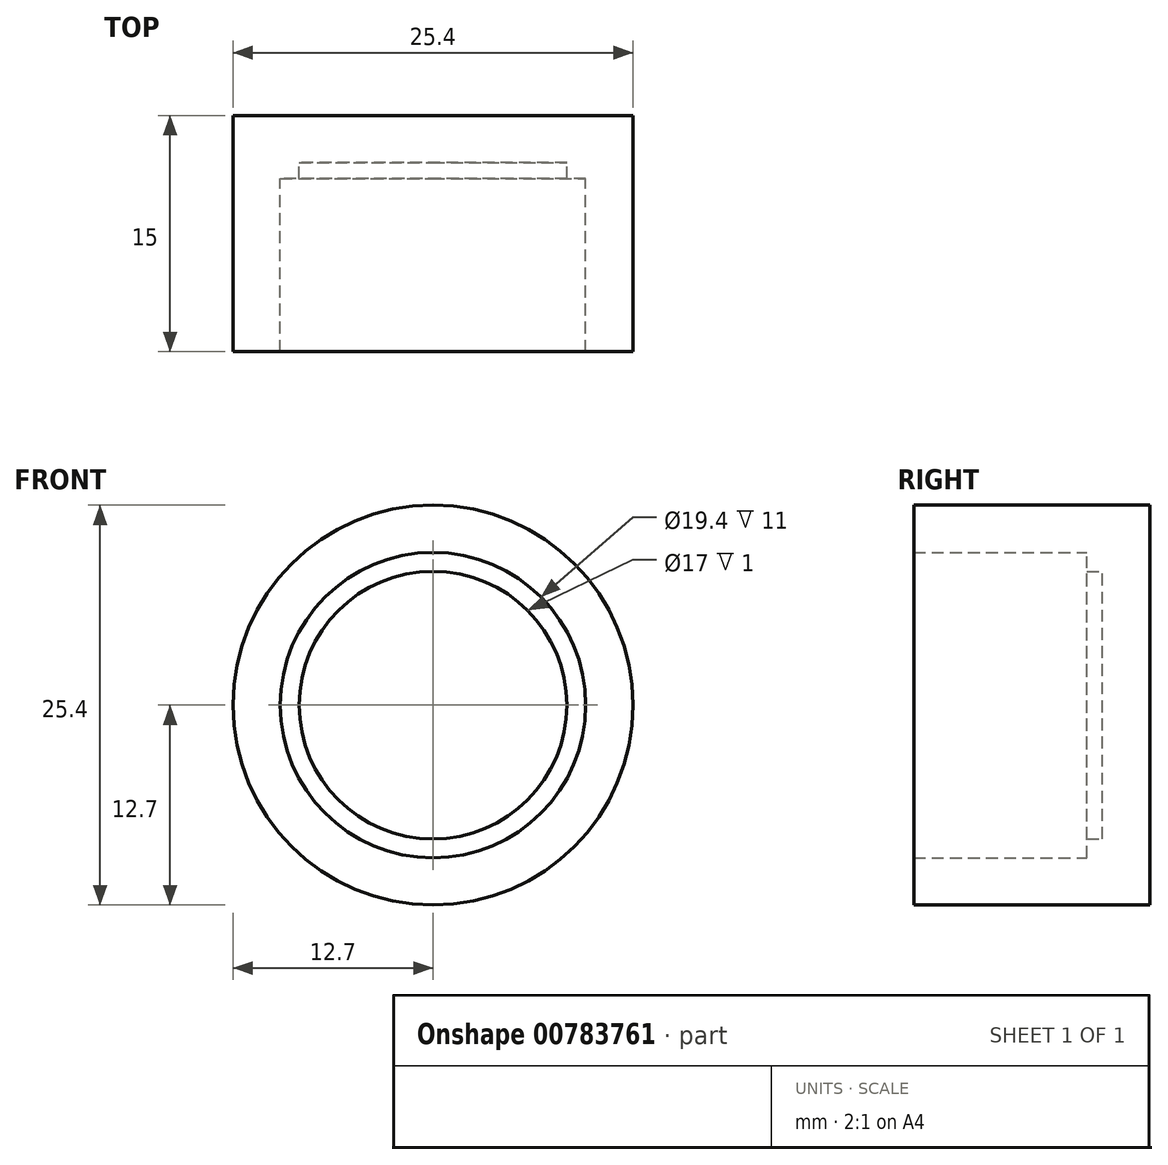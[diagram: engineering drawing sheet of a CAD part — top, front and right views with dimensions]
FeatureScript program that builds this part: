
annotation { "Feature Type Name" : "Feature", "Feature Type Description" : "" }
export const myFeature = defineFeature(function(context is Context, id is Id, definition is map)
    precondition{}
    {
        {
            var Q0;
            Q0=qCreatedBy(makeId("Front.planeOp"),FACE);
            var sketch = newSketch(context, id + "F0", { "sketchPlane" : qUnion([Q0])});
            skCircle(sketch, "E0", {"center": v(0, 0) * mm, "radius": 12.7 * mm});
            skCircle(sketch, "E1", {"center": v(0, 0) * mm, "radius": 9.7 * mm});
            skCircle(sketch, "E2", {"center": v(0, 0) * mm, "radius": 8.5 * mm});
            skSolve(sketch);
        }
        {
            var Q0;
            Q0=makeQuery(id+"F0.imprint","IMPRINT",FACE,{"disambiguationData":[TD([[makeQuery(id+"F0.imprint","IMPRINT",EDGE,{"derivedFrom":sQuery(id+"F0.wireOp",EDGE,"E0")}),1.0]])]});
            extrude(context, id + "F1", {"entities" : qUnion([Q0]), "depth" : 12 * mm, "offsetDistance" : 25 * mm, "hasSecondDirection" : true, "secondDirectionOppositeDirection" : true, "secondDirectionDepth" : 3 * mm});
        }
        {
            var Q0;
            Q0=makeQuery(id+"F0.imprint","IMPRINT",FACE,{"disambiguationData":[TD([[makeQuery(id+"F0.imprint","IMPRINT",EDGE,{"derivedFrom":sQuery(id+"F0.wireOp",EDGE,"E1")}),1.0]])]});
            extrude(context, id + "F2", {"entities" : qUnion([Q0]), "depth" : 1 * mm, "offsetDistance" : 25 * mm});
        }
        {
            var Q0;
            Q0 = qSketchRegion(id + "F0", true);
            var Q1;
            Q1=makeQuery(id+"F0.imprint","IMPRINT",FACE,{"disambiguationData":[TD([[makeQuery(id+"F0.imprint","IMPRINT",EDGE,{"derivedFrom":sQuery(id+"F0.wireOp",EDGE,"E1")}),1.0]])]});
            var Q2;
            Q2=makeQuery(id+"F0.imprint","IMPRINT",FACE,{"disambiguationData":[TD([[makeQuery(id+"F0.imprint","IMPRINT",EDGE,{"derivedFrom":sQuery(id+"F0.wireOp",EDGE,"E2")}),1.0]])]});
            extrude(context, id + "F3", {"entities" : qUnion([Q0, Q1, Q2]), "operationType" : NewBodyOperationType.ADD, "oppositeDirection" : true, "depth" : 3 * mm, "offsetDistance" : 25 * mm});
        }
    });
